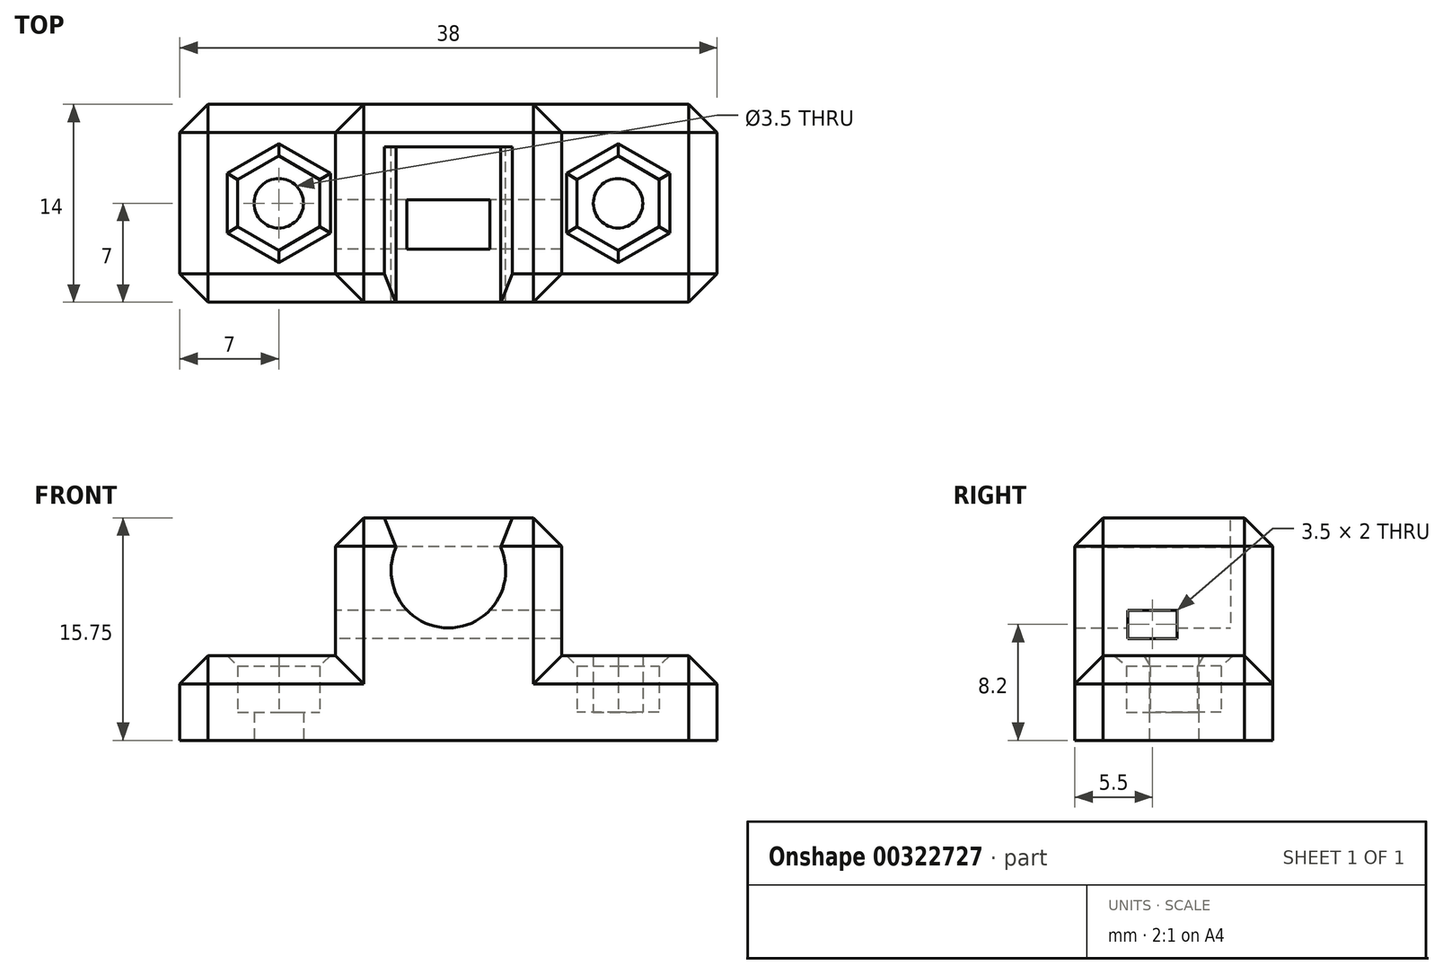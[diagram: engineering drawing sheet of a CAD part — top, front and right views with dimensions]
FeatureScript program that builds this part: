
annotation { "Feature Type Name" : "Feature", "Feature Type Description" : "" }
export const myFeature = defineFeature(function(context is Context, id is Id, definition is map)
    precondition{}
    {
        {
            var Q0;
            Q0=qCreatedBy(makeId("Front.planeOp"),FACE);
            var sketch = newSketch(context, id + "F0", { "sketchPlane" : qUnion([Q0])});
            skLineSegment(sketch, "E0", {"start": v(0, 0) * mm, "end": v(-19, 0) * mm});
            skLineSegment(sketch, "E1", {"start": v(-19, 0) * mm, "end": v(-19, 6) * mm});
            skLineSegment(sketch, "E2", {"start": v(-19, 6) * mm, "end": v(-8, 6) * mm});
            skLineSegment(sketch, "E3", {"start": v(-8, 6) * mm, "end": v(-8, 15.75) * mm});
            skLineSegment(sketch, "E4", {"start": v(-8, 15.75) * mm, "end": v(0, 15.75) * mm});
            skLineSegment(sketch, "E5.MirrorCS", {"start": v(0, 0) * mm, "end": v(19, 0) * mm});
            skLineSegment(sketch, "E6.MirrorCS", {"start": v(19, 6) * mm, "end": v(8, 6) * mm});
            skLineSegment(sketch, "E7.MirrorCS", {"start": v(8, 15.75) * mm, "end": v(0, 15.75) * mm});
            skLineSegment(sketch, "E8.MirrorCS", {"start": v(8, 6) * mm, "end": v(8, 15.75) * mm});
            skLineSegment(sketch, "E9.MirrorCS", {"start": v(19, 0) * mm, "end": v(19, 6) * mm});
            skCircle(sketch, "E10", {"center": v(0, 12) * mm, "radius": 4.05 * mm});
            skSolve(sketch);
        }
        {
            var Q0;
            Q0=makeQuery(id+"F0.imprint","IMPRINT",FACE,{"disambiguationData":[TD([[makeQuery(id+"F0.imprint","IMPRINT",EDGE,{"derivedFrom":sQuery(id+"F0.wireOp",EDGE,"E0")}),-1.0]])]});
            var Q1;
            {var subQ0=sQuery(id+"F0.wireOp",EDGE,"E7.MirrorCS");var subQ1=sQuery(id+"F0.wireOp",EDGE,"E4");var subQ2=makeQuery(id+"F0.imprint","INTERSECT",VERTEX,{"derivedFrom":[subQ1,subQ0]});Q1=makeQuery(id+"F0.imprint","IMPRINT",FACE,{"disambiguationData":[TD([[makeQuery(id+"F0.imprint","IMPRINT",EDGE,{"disambiguationData":[TD([[subQ2,1.0]])],"derivedFrom":subQ1}),-1.0]])]});}
            extrude(context, id + "F1", {"entities" : qUnion([Q0, Q1]), "oppositeDirection" : true, "depth" : 3 * mm});
        }
        {
            var Q0;
            Q0=makeQuery(id+"F0.imprint","IMPRINT",FACE,{"disambiguationData":[TD([[makeQuery(id+"F0.imprint","IMPRINT",EDGE,{"derivedFrom":sQuery(id+"F0.wireOp",EDGE,"E0")}),-1.0]])]});
            extrude(context, id + "F2", {"entities" : qUnion([Q0]), "operationType" : NewBodyOperationType.ADD, "depth" : 11 * mm});
        }
        {
            var Q0;
            {var subQ0=sQuery(id+"F0.wireOp",EDGE,"E3");Q0=makeQuery(id+"F2.boolean.opBoolean","MERGE",FACE,{"derivedFrom":[makeQuery(id+"F1.opExtrude","SWEPT_FACE",FACE,{"disambiguationData":[OSD([subQ0])]}),makeQuery(id+"F2.opExtrude","SWEPT_FACE",FACE,{"disambiguationData":[OSD([subQ0])]})]});}
            var sketch = newSketch(context, id + "F3", { "sketchPlane" : qUnion([Q0])});
            skLineSegment(sketch, "E11.bottom", {"start": v(3.75, 9.2) * mm, "end": v(7.25, 9.2) * mm});
            skLineSegment(sketch, "E11.top", {"start": v(3.75, 7.2) * mm, "end": v(7.25, 7.2) * mm});
            skLineSegment(sketch, "E11.left", {"start": v(3.75, 9.2) * mm, "end": v(3.75, 7.2) * mm});
            skLineSegment(sketch, "E11.right", {"start": v(7.25, 9.2) * mm, "end": v(7.25, 7.2) * mm});
            skSolve(sketch);
        }
        {
            var Q0;
            Q0=makeQuery(id+"F3.imprint","IMPRINT",FACE,{"disambiguationData":[TD([[makeQuery(id+"F3.imprint","IMPRINT",EDGE,{"derivedFrom":sQuery(id+"F3.wireOp",EDGE,"E11.bottom")}),-1.0]])]});
            extrude(context, id + "F4", {"entities" : qUnion([Q0]), "operationType" : NewBodyOperationType.REMOVE, "endBound" : BoundingType.THROUGH_ALL, "oppositeDirection" : true, "depth" : 25 * mm});
        }
        {
            var Q0;
            {var subQ0=sQuery(id+"F0.wireOp",EDGE,"E5.MirrorCS");var subQ1=sQuery(id+"F0.wireOp",EDGE,"E0");Q0=makeQuery(id+"F2.boolean.opBoolean","MERGE",FACE,{"derivedFrom":[makeQuery(id+"F1.opExtrude","SWEPT_FACE",FACE,{"disambiguationData":[OSD([subQ1,subQ0])]}),makeQuery(id+"F2.opExtrude","SWEPT_FACE",FACE,{"disambiguationData":[OSD([subQ1,subQ0])]})]});}
            var sketch = newSketch(context, id + "F5", { "sketchPlane" : qUnion([Q0])});
            skCircle(sketch, "E12", {"center": v(-12, 4) * mm, "radius": 1.75 * mm});
            skPoint(sketch, "E12.centerSnap0", {"position": v(-19, 4) * mm});
            skCircle(sketch, "E13.cCircle", {"center": v(-12, 4) * mm, "radius": 2.9 * mm, "construction": true});
            skLineSegment(sketch, "E13.0", {"start": v(-9.1, 5.67) * mm, "end": v(-9.1, 2.33) * mm});
            skLineSegment(sketch, "E13.1", {"start": v(-9.1, 2.33) * mm, "end": v(-12, 0.65) * mm});
            skLineSegment(sketch, "E13.2", {"start": v(-12, 0.65) * mm, "end": v(-14.9, 2.33) * mm});
            skLineSegment(sketch, "E13.3", {"start": v(-14.9, 2.33) * mm, "end": v(-14.9, 5.67) * mm});
            skLineSegment(sketch, "E13.4", {"start": v(-14.9, 5.67) * mm, "end": v(-12, 7.35) * mm});
            skLineSegment(sketch, "E13.5", {"start": v(-12, 7.35) * mm, "end": v(-9.1, 5.67) * mm});
            skPoint(sketch, "E13.0.midPoint", {"position": v(-9.1, 4) * mm});
            skLineSegment(sketch, "E14.MirrorCS", {"start": v(9.1, 2.33) * mm, "end": v(12, 0.65) * mm});
            skCircle(sketch, "E15.MirrorC", {"center": v(12, 4) * mm, "radius": 2.9 * mm, "construction": true});
            skCircle(sketch, "E16.MirrorC", {"center": v(12, 4) * mm, "radius": 1.75 * mm});
            skLineSegment(sketch, "E17.MirrorCS", {"start": v(9.1, 5.67) * mm, "end": v(9.1, 2.33) * mm});
            skLineSegment(sketch, "E18.MirrorCS", {"start": v(12, 7.35) * mm, "end": v(9.1, 5.67) * mm});
            skLineSegment(sketch, "E19.MirrorCS", {"start": v(14.9, 2.33) * mm, "end": v(14.9, 5.67) * mm});
            skPoint(sketch, "E20.MirrorP", {"position": v(9.1, 4) * mm});
            skLineSegment(sketch, "E21.MirrorCS", {"start": v(12, 0.65) * mm, "end": v(14.9, 2.33) * mm});
            skLineSegment(sketch, "E22.MirrorCS", {"start": v(14.9, 5.67) * mm, "end": v(12, 7.35) * mm});
            skSolve(sketch);
        }
        {
            var Q0;
            Q0=makeQuery(id+"F5.imprint","IMPRINT",FACE,{"disambiguationData":[TD([[makeQuery(id+"F5.imprint","IMPRINT",EDGE,{"derivedFrom":sQuery(id+"F5.wireOp",EDGE,"E14.MirrorCS")}),1.0]])]});
            var Q1;
            Q1=makeQuery(id+"F5.imprint","IMPRINT",FACE,{"disambiguationData":[TD([[makeQuery(id+"F5.imprint","IMPRINT",EDGE,{"derivedFrom":sQuery(id+"F5.wireOp",EDGE,"E16.MirrorC")}),-1.0]])]});
            var Q2;
            Q2=makeQuery(id+"F5.imprint","IMPRINT",FACE,{"disambiguationData":[TD([[makeQuery(id+"F5.imprint","IMPRINT",EDGE,{"derivedFrom":sQuery(id+"F5.wireOp",EDGE,"E12")}),1.0]])]});
            var Q3;
            Q3=makeQuery(id+"F5.imprint","IMPRINT",FACE,{"disambiguationData":[TD([[makeQuery(id+"F5.imprint","IMPRINT",EDGE,{"derivedFrom":sQuery(id+"F5.wireOp",EDGE,"E12")}),-1.0]])]});
            extrude(context, id + "F6", {"entities" : qUnion([Q0, Q1, Q2, Q3]), "operationType" : NewBodyOperationType.REMOVE, "oppositeDirection" : true, "depth" : 25 * mm});
        }
        {
            var Q0;
            Q0=makeQuery(id+"F5.imprint","IMPRINT",FACE,{"disambiguationData":[TD([[makeQuery(id+"F5.imprint","IMPRINT",EDGE,{"derivedFrom":sQuery(id+"F5.wireOp",EDGE,"E14.MirrorCS")}),1.0]])]});
            var Q1;
            Q1=makeQuery(id+"F5.imprint","IMPRINT",FACE,{"disambiguationData":[TD([[makeQuery(id+"F5.imprint","IMPRINT",EDGE,{"derivedFrom":sQuery(id+"F5.wireOp",EDGE,"E12")}),-1.0]])]});
            extrude(context, id + "F7", {"entities" : qUnion([Q0, Q1]), "operationType" : NewBodyOperationType.ADD, "oppositeDirection" : true, "depth" : 2 * mm});
        }
        {
            var Q0;
            Q0=makeQuery(id+"F2.opExtrude","CAP_EDGE",EDGE,{"disambiguationData":[OSD([sQuery(id+"F0.wireOp",EDGE,"E2")])],"isStart":false});
            var Q1;
            Q1=makeQuery(id+"F2.opExtrude","CAP_EDGE",EDGE,{"disambiguationData":[OSD([sQuery(id+"F0.wireOp",EDGE,"E6.MirrorCS")])],"isStart":false});
            var Q2;
            Q2=makeQuery(id+"F2.opExtrude","CAP_EDGE",EDGE,{"disambiguationData":[OSD([sQuery(id+"F0.wireOp",EDGE,"E9.MirrorCS")])],"isStart":false});
            var Q3;
            {var subQ0=sQuery(id+"F0.wireOp",EDGE,"E9.MirrorCS");var subQ1=sQuery(id+"F0.wireOp",EDGE,"E6.MirrorCS");Q3=makeQuery(id+"F2.boolean.opBoolean","MERGE",EDGE,{"derivedFrom":[makeQuery(id+"F1.opExtrude","SWEPT_EDGE",EDGE,{"disambiguationData":[OSD([subQ1,subQ0])]}),makeQuery(id+"F2.opExtrude","SWEPT_EDGE",EDGE,{"disambiguationData":[OSD([subQ1,subQ0])]})]});}
            var Q4;
            Q4=makeQuery(id+"F1.opExtrude","CAP_EDGE",EDGE,{"disambiguationData":[OSD([sQuery(id+"F0.wireOp",EDGE,"E6.MirrorCS")])],"isStart":false});
            var Q5;
            Q5=makeQuery(id+"F2.opExtrude","CAP_EDGE",EDGE,{"disambiguationData":[OSD([sQuery(id+"F0.wireOp",EDGE,"E8.MirrorCS")])],"isStart":false});
            var Q6;
            Q6=makeQuery(id+"F1.opExtrude","CAP_EDGE",EDGE,{"disambiguationData":[OSD([sQuery(id+"F0.wireOp",EDGE,"E8.MirrorCS")])],"isStart":false});
            var Q7;
            Q7=makeQuery(id+"F2.opExtrude","CAP_EDGE",EDGE,{"disambiguationData":[OSD([sQuery(id+"F0.wireOp",EDGE,"E3")])],"isStart":false});
            var Q8;
            Q8=makeQuery(id+"F1.opExtrude","CAP_EDGE",EDGE,{"disambiguationData":[OSD([sQuery(id+"F0.wireOp",EDGE,"E3")])],"isStart":false});
            var Q9;
            {var subQ0=sQuery(id+"F0.wireOp",EDGE,"E2");var subQ1=sQuery(id+"F0.wireOp",EDGE,"E1");Q9=makeQuery(id+"F2.boolean.opBoolean","MERGE",EDGE,{"derivedFrom":[makeQuery(id+"F1.opExtrude","SWEPT_EDGE",EDGE,{"disambiguationData":[OSD([subQ1,subQ0])]}),makeQuery(id+"F2.opExtrude","SWEPT_EDGE",EDGE,{"disambiguationData":[OSD([subQ1,subQ0])]})]});}
            var Q10;
            Q10=makeQuery(id+"F1.opExtrude","CAP_EDGE",EDGE,{"disambiguationData":[OSD([sQuery(id+"F0.wireOp",EDGE,"E1")])],"isStart":false});
            var Q11;
            Q11=makeQuery(id+"F1.opExtrude","CAP_EDGE",EDGE,{"disambiguationData":[OSD([sQuery(id+"F0.wireOp",EDGE,"E2")])],"isStart":false});
            var Q12;
            {var subQ0=sQuery(id+"F0.wireOp",EDGE,"E4");var subQ1=sQuery(id+"F0.wireOp",EDGE,"E3");Q12=makeQuery(id+"F2.boolean.opBoolean","MERGE",EDGE,{"derivedFrom":[makeQuery(id+"F1.opExtrude","SWEPT_EDGE",EDGE,{"disambiguationData":[OSD([subQ1,subQ0])]}),makeQuery(id+"F2.opExtrude","SWEPT_EDGE",EDGE,{"disambiguationData":[OSD([subQ1,subQ0])]})]});}
            var Q13;
            {var subQ0=sQuery(id+"F0.wireOp",EDGE,"E8.MirrorCS");var subQ1=sQuery(id+"F0.wireOp",EDGE,"E7.MirrorCS");Q13=makeQuery(id+"F2.boolean.opBoolean","MERGE",EDGE,{"derivedFrom":[makeQuery(id+"F1.opExtrude","SWEPT_EDGE",EDGE,{"disambiguationData":[OSD([subQ1,subQ0])]}),makeQuery(id+"F2.opExtrude","SWEPT_EDGE",EDGE,{"disambiguationData":[OSD([subQ1,subQ0])]})]});}
            var Q14;
            Q14=makeQuery(id+"F1.opExtrude","CAP_EDGE",EDGE,{"disambiguationData":[OSD([sQuery(id+"F0.wireOp",EDGE,"E4"),sQuery(id+"F0.wireOp",EDGE,"E7.MirrorCS")])],"isStart":false});
            var Q15;
            Q15=makeQuery(id+"F1.opExtrude","CAP_EDGE",EDGE,{"disambiguationData":[OSD([sQuery(id+"F0.wireOp",EDGE,"E9.MirrorCS")])],"isStart":false});
            var Q16;
            Q16=makeQuery(id+"F2.opExtrude","CAP_EDGE",EDGE,{"disambiguationData":[OSD([sQuery(id+"F0.wireOp",EDGE,"E1")])],"isStart":false});
            var Q17;
            Q17=makeQuery(id+"F2.opExtrude","CAP_EDGE",EDGE,{"disambiguationData":[OSD([sQuery(id+"F0.wireOp",EDGE,"E7.MirrorCS")])],"isStart":false});
            var Q18;
            Q18=makeQuery(id+"F2.opExtrude","CAP_EDGE",EDGE,{"disambiguationData":[OSD([sQuery(id+"F0.wireOp",EDGE,"E4")])],"isStart":false});
            chamfer(context, id + "F8", {"entities" : qUnion([Q0, Q1, Q2, Q3, Q4, Q5, Q6, Q7, Q8, Q9, Q10, Q11, Q12, Q13, Q14, Q15, Q16, Q17, Q18]), "width" : 2 * mm, "tangentPropagation" : true});
        }
        {
            var Q0;
            Q0=makeQuery(id+"F2.opExtrude","SWEPT_EDGE",EDGE,{"disambiguationData":[OSD([sQuery(id+"F0.wireOp",EDGE,"E4"),sQuery(id+"F0.wireOp",EDGE,"E10")])]});
            var Q1;
            Q1=makeQuery(id+"F2.opExtrude","SWEPT_EDGE",EDGE,{"disambiguationData":[OSD([sQuery(id+"F0.wireOp",EDGE,"E7.MirrorCS"),sQuery(id+"F0.wireOp",EDGE,"E10")])]});
            chamfer(context, id + "F9", {"entities" : qUnion([Q0, Q1]), "width" : 3 * mm, "tangentPropagation" : true});
        }
        {
            var Q0;
            {var subQ0=sQuery(id+"F0.wireOp",EDGE,"E6.MirrorCS");Q0=makeQuery(id+"F6.boolean.opBoolean","INTERSECT",EDGE,{"derivedFrom":[makeQuery(id+"F2.boolean.opBoolean","MERGE",FACE,{"derivedFrom":[makeQuery(id+"F1.opExtrude","SWEPT_FACE",FACE,{"disambiguationData":[OSD([subQ0])]}),makeQuery(id+"F2.opExtrude","SWEPT_FACE",FACE,{"disambiguationData":[OSD([subQ0])]})]}),makeQuery(id+"F6.opExtrude","SWEPT_FACE",FACE,{"disambiguationData":[OSD([sQuery(id+"F5.wireOp",EDGE,"E17.MirrorCS")])]})]});}
            var Q1;
            {var subQ0=sQuery(id+"F0.wireOp",EDGE,"E6.MirrorCS");Q1=makeQuery(id+"F6.boolean.opBoolean","INTERSECT",EDGE,{"derivedFrom":[makeQuery(id+"F2.boolean.opBoolean","MERGE",FACE,{"derivedFrom":[makeQuery(id+"F1.opExtrude","SWEPT_FACE",FACE,{"disambiguationData":[OSD([subQ0])]}),makeQuery(id+"F2.opExtrude","SWEPT_FACE",FACE,{"disambiguationData":[OSD([subQ0])]})]}),makeQuery(id+"F6.opExtrude","SWEPT_FACE",FACE,{"disambiguationData":[OSD([sQuery(id+"F5.wireOp",EDGE,"E14.MirrorCS")])]})]});}
            var Q2;
            {var subQ0=sQuery(id+"F0.wireOp",EDGE,"E6.MirrorCS");Q2=makeQuery(id+"F6.boolean.opBoolean","INTERSECT",EDGE,{"derivedFrom":[makeQuery(id+"F2.boolean.opBoolean","MERGE",FACE,{"derivedFrom":[makeQuery(id+"F1.opExtrude","SWEPT_FACE",FACE,{"disambiguationData":[OSD([subQ0])]}),makeQuery(id+"F2.opExtrude","SWEPT_FACE",FACE,{"disambiguationData":[OSD([subQ0])]})]}),makeQuery(id+"F6.opExtrude","SWEPT_FACE",FACE,{"disambiguationData":[OSD([sQuery(id+"F5.wireOp",EDGE,"E21.MirrorCS")])]})]});}
            var Q3;
            {var subQ0=sQuery(id+"F0.wireOp",EDGE,"E6.MirrorCS");Q3=makeQuery(id+"F6.boolean.opBoolean","INTERSECT",EDGE,{"derivedFrom":[makeQuery(id+"F2.boolean.opBoolean","MERGE",FACE,{"derivedFrom":[makeQuery(id+"F1.opExtrude","SWEPT_FACE",FACE,{"disambiguationData":[OSD([subQ0])]}),makeQuery(id+"F2.opExtrude","SWEPT_FACE",FACE,{"disambiguationData":[OSD([subQ0])]})]}),makeQuery(id+"F6.opExtrude","SWEPT_FACE",FACE,{"disambiguationData":[OSD([sQuery(id+"F5.wireOp",EDGE,"E19.MirrorCS")])]})]});}
            var Q4;
            {var subQ0=sQuery(id+"F0.wireOp",EDGE,"E6.MirrorCS");Q4=makeQuery(id+"F6.boolean.opBoolean","INTERSECT",EDGE,{"derivedFrom":[makeQuery(id+"F2.boolean.opBoolean","MERGE",FACE,{"derivedFrom":[makeQuery(id+"F1.opExtrude","SWEPT_FACE",FACE,{"disambiguationData":[OSD([subQ0])]}),makeQuery(id+"F2.opExtrude","SWEPT_FACE",FACE,{"disambiguationData":[OSD([subQ0])]})]}),makeQuery(id+"F6.opExtrude","SWEPT_FACE",FACE,{"disambiguationData":[OSD([sQuery(id+"F5.wireOp",EDGE,"E22.MirrorCS")])]})]});}
            var Q5;
            {var subQ0=sQuery(id+"F0.wireOp",EDGE,"E6.MirrorCS");Q5=makeQuery(id+"F6.boolean.opBoolean","INTERSECT",EDGE,{"derivedFrom":[makeQuery(id+"F2.boolean.opBoolean","MERGE",FACE,{"derivedFrom":[makeQuery(id+"F1.opExtrude","SWEPT_FACE",FACE,{"disambiguationData":[OSD([subQ0])]}),makeQuery(id+"F2.opExtrude","SWEPT_FACE",FACE,{"disambiguationData":[OSD([subQ0])]})]}),makeQuery(id+"F6.opExtrude","SWEPT_FACE",FACE,{"disambiguationData":[OSD([sQuery(id+"F5.wireOp",EDGE,"E18.MirrorCS")])]})]});}
            var Q6;
            {var subQ0=sQuery(id+"F0.wireOp",EDGE,"E2");Q6=makeQuery(id+"F6.boolean.opBoolean","INTERSECT",EDGE,{"derivedFrom":[makeQuery(id+"F2.boolean.opBoolean","MERGE",FACE,{"derivedFrom":[makeQuery(id+"F1.opExtrude","SWEPT_FACE",FACE,{"disambiguationData":[OSD([subQ0])]}),makeQuery(id+"F2.opExtrude","SWEPT_FACE",FACE,{"disambiguationData":[OSD([subQ0])]})]}),makeQuery(id+"F6.opExtrude","SWEPT_FACE",FACE,{"disambiguationData":[OSD([sQuery(id+"F5.wireOp",EDGE,"E13.2")])]})]});}
            var Q7;
            {var subQ0=sQuery(id+"F0.wireOp",EDGE,"E2");Q7=makeQuery(id+"F6.boolean.opBoolean","INTERSECT",EDGE,{"derivedFrom":[makeQuery(id+"F2.boolean.opBoolean","MERGE",FACE,{"derivedFrom":[makeQuery(id+"F1.opExtrude","SWEPT_FACE",FACE,{"disambiguationData":[OSD([subQ0])]}),makeQuery(id+"F2.opExtrude","SWEPT_FACE",FACE,{"disambiguationData":[OSD([subQ0])]})]}),makeQuery(id+"F6.opExtrude","SWEPT_FACE",FACE,{"disambiguationData":[OSD([sQuery(id+"F5.wireOp",EDGE,"E13.1")])]})]});}
            var Q8;
            {var subQ0=sQuery(id+"F0.wireOp",EDGE,"E2");Q8=makeQuery(id+"F6.boolean.opBoolean","INTERSECT",EDGE,{"derivedFrom":[makeQuery(id+"F2.boolean.opBoolean","MERGE",FACE,{"derivedFrom":[makeQuery(id+"F1.opExtrude","SWEPT_FACE",FACE,{"disambiguationData":[OSD([subQ0])]}),makeQuery(id+"F2.opExtrude","SWEPT_FACE",FACE,{"disambiguationData":[OSD([subQ0])]})]}),makeQuery(id+"F6.opExtrude","SWEPT_FACE",FACE,{"disambiguationData":[OSD([sQuery(id+"F5.wireOp",EDGE,"E13.0")])]})]});}
            var Q9;
            {var subQ0=sQuery(id+"F0.wireOp",EDGE,"E2");Q9=makeQuery(id+"F6.boolean.opBoolean","INTERSECT",EDGE,{"derivedFrom":[makeQuery(id+"F2.boolean.opBoolean","MERGE",FACE,{"derivedFrom":[makeQuery(id+"F1.opExtrude","SWEPT_FACE",FACE,{"disambiguationData":[OSD([subQ0])]}),makeQuery(id+"F2.opExtrude","SWEPT_FACE",FACE,{"disambiguationData":[OSD([subQ0])]})]}),makeQuery(id+"F6.opExtrude","SWEPT_FACE",FACE,{"disambiguationData":[OSD([sQuery(id+"F5.wireOp",EDGE,"E13.5")])]})]});}
            var Q10;
            {var subQ0=sQuery(id+"F0.wireOp",EDGE,"E2");Q10=makeQuery(id+"F6.boolean.opBoolean","INTERSECT",EDGE,{"derivedFrom":[makeQuery(id+"F2.boolean.opBoolean","MERGE",FACE,{"derivedFrom":[makeQuery(id+"F1.opExtrude","SWEPT_FACE",FACE,{"disambiguationData":[OSD([subQ0])]}),makeQuery(id+"F2.opExtrude","SWEPT_FACE",FACE,{"disambiguationData":[OSD([subQ0])]})]}),makeQuery(id+"F6.opExtrude","SWEPT_FACE",FACE,{"disambiguationData":[OSD([sQuery(id+"F5.wireOp",EDGE,"E13.3")])]})]});}
            var Q11;
            {var subQ0=sQuery(id+"F0.wireOp",EDGE,"E2");Q11=makeQuery(id+"F6.boolean.opBoolean","INTERSECT",EDGE,{"derivedFrom":[makeQuery(id+"F2.boolean.opBoolean","MERGE",FACE,{"derivedFrom":[makeQuery(id+"F1.opExtrude","SWEPT_FACE",FACE,{"disambiguationData":[OSD([subQ0])]}),makeQuery(id+"F2.opExtrude","SWEPT_FACE",FACE,{"disambiguationData":[OSD([subQ0])]})]}),makeQuery(id+"F6.opExtrude","SWEPT_FACE",FACE,{"disambiguationData":[OSD([sQuery(id+"F5.wireOp",EDGE,"E13.4")])]})]});}
            chamfer(context, id + "F10", {"entities" : qUnion([Q0, Q1, Q2, Q3, Q4, Q5, Q6, Q7, Q8, Q9, Q10, Q11]), "width" : 0.75 * mm, "tangentPropagation" : true});
        }
    });
